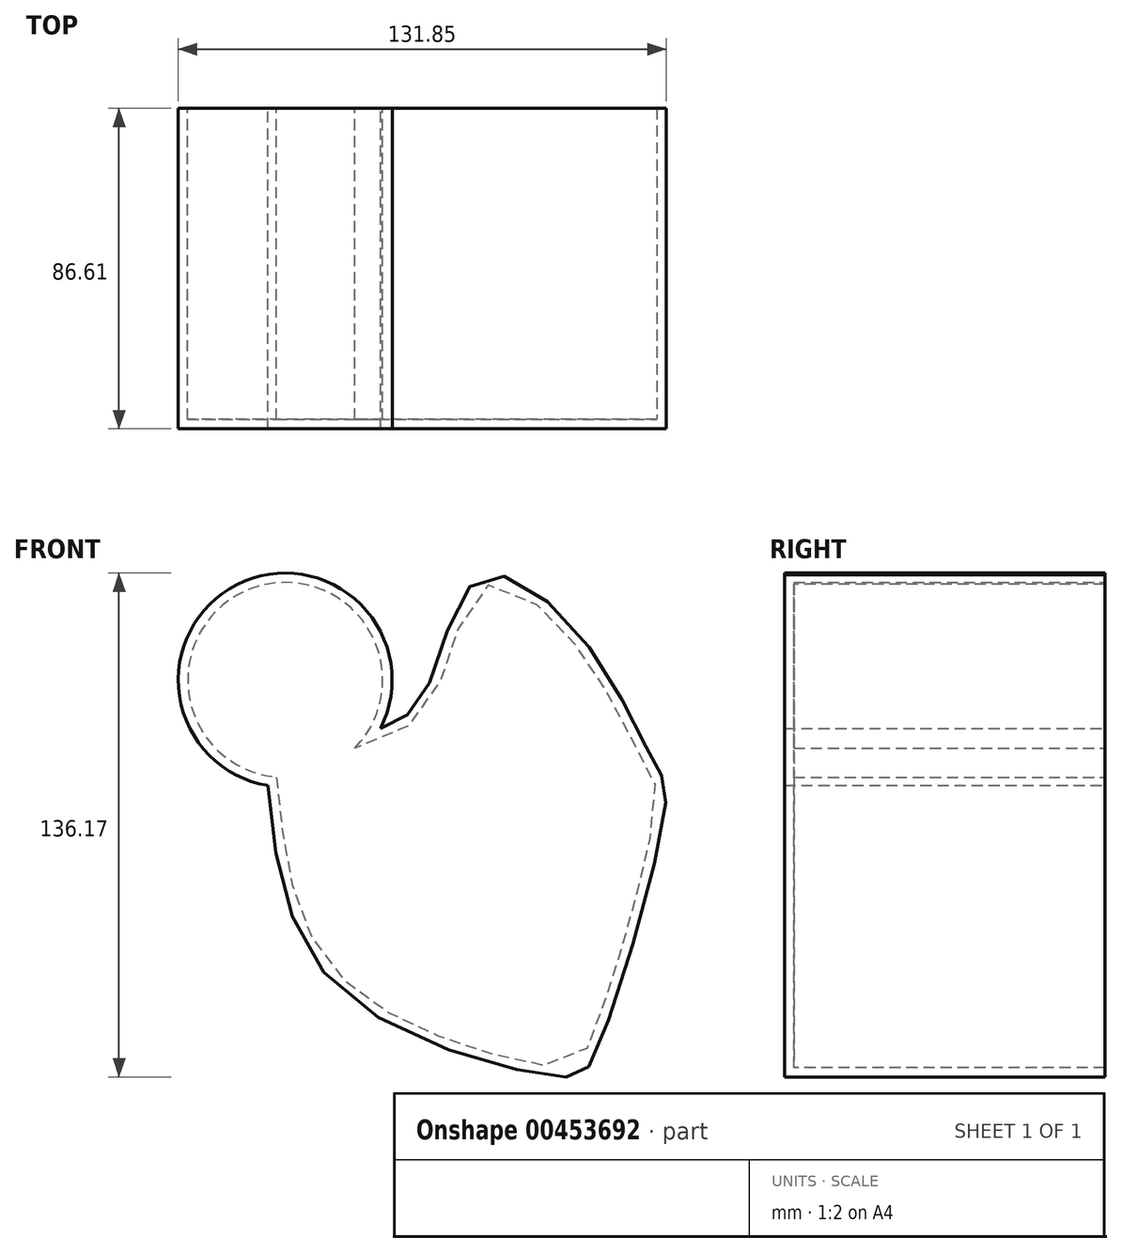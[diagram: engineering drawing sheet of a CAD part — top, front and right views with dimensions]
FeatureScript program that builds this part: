
annotation { "Feature Type Name" : "Feature", "Feature Type Description" : "" }
export const myFeature = defineFeature(function(context is Context, id is Id, definition is map)
    precondition{}
    {
        {
            var Q0;
            Q0=qCreatedBy(makeId("Front.planeOp"),FACE);
            var sketch = newSketch(context, id + "F0", { "sketchPlane" : qUnion([Q0])});
            skCircle(sketch, "E0", {"center": v(-62.65, 50.83) * mm, "radius": 28.9 * mm});
            skFitSpline(sketch, "E1", {"points": [v(-67.37, 22.32) * mm, v(-47.15, -33.4) * mm, v(12.53, -56.4) * mm, v(20.77, -51.05) * mm, v(40.23, 18.2) * mm, v(37.6, 27.67) * mm, v(16.82, 63.22) * mm, v(-10.55, 78.07) * mm, v(-25.4, 46.42) * mm, v(-36.89, 37.74) * mm], "startDerivative": vector(43.07, -422.2) * mm, "endDerivative": vector(-171.13, -64.58) * mm});
            skSolve(sketch);
        }
        {
            var Q0;
            {var subQ0=sQuery(id+"F0.wireOp",EDGE,"E1");Q0=makeQuery(id+"F0.imprint","IMPRINT",FACE,{"disambiguationData":[TD([[makeQuery(id+"F0.imprint","IMPRINT",EDGE,{"derivedFrom":subQ0}),1.0]])]});}
            var Q1;
            {var subQ0=sQuery(id+"F0.wireOp",EDGE,"E1");var subQ1=sQuery(id+"F0.wireOp",EDGE,"E0");var subQ2=makeQuery(id+"F0.imprint","INTERSECT",VERTEX,{"disambiguationData":[OD(0.0)],"derivedFrom":[subQ1,subQ0]});Q1=makeQuery(id+"F0.imprint","IMPRINT",FACE,{"disambiguationData":[TD([[makeQuery(id+"F0.imprint","IMPRINT",EDGE,{"disambiguationData":[TD([[subQ2,-1.0]])],"derivedFrom":subQ1}),1.0]])]});}
            extrude(context, id + "F1", {"entities" : qUnion([Q0, Q1]), "depth" : 86.61 * mm});
        }
        {
            var Q0;
            Q0=qCreatedBy(makeId("Top.planeOp"),FACE);
            var sketch = newSketch(context, id + "F2", { "sketchPlane" : qUnion([Q0])});
            skLineSegment(sketch, "E2", {"start": v(-182.12, -69.16) * mm, "end": v(-182.12, 101.82) * mm});
            skLineSegment(sketch, "E3", {"start": v(-97.94, 148.06) * mm, "end": v(-138.7, 147.41) * mm});
            skSolve(sketch);
        }
        {
            var Q0;
            Q0=makeQuery(id+"F1.opExtrude","CAP_FACE",FACE,{"disambiguationData":[OSD([sQuery(id+"F0.wireOp",EDGE,"E0"),sQuery(id+"F0.wireOp",EDGE,"E1")])],"isStart":true});
            shell(context, id + "F3", {"entities" : qUnion([Q0]), "thickness" : 2.54 * mm});
        }
    });
